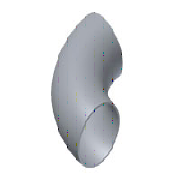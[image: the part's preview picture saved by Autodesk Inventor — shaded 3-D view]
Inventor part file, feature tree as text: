
AUTODESK INVENTOR PART (.ipt)
format: ipt  version: 2023 (Build 270158000, 158)  size: 178,688 bytes
history: native  units: mm
features: other x4, sketch x2, sweep x1
ambient origin geometry x8: Origin, YZ Plane, XZ Plane, XY Plane, X Axis, Y Axis, Z Axis, Center Point
bodies: Solid1 (feature_tree)
feature tree (7):
  sweep  "Колебание1"
  other  "Work Axis1"
  other  "Work Axis2"
  sketch  "Sketch1"  dims[d2=108.0mm d3=4.0mm]
  sketch  "Sketch2"  dims[d4=150.0mm d5=300.0mm d6=0.0mm d7=90.0deg d8=0.0mm]
  other  "Work Point1"
  other  "Work Point2"
